# Revit family: QF_Vollrath_K1410-C
name_source: partatom
category: Specialty Equipment
revit_build: Autodesk Revit 2016 (Build: 20151007_0715(x64)
units: mm (PartAtom-declared; Revit-internal decimal feet)

## family parameters
Always vertical = Yes
Cut with Voids When Loaded = No
OmniClass Number = 23.40.40.14.31
OmniClass Title = Cleaning and Disposal Equipment
Part Type = Normal
Room Calculation Point = No
Round Connector Dimension = Use Diameter
Shared = No
Work Plane-Based = Yes

## types (1)
- QF_Vollrath_K1410-C
    Cold Water Size = 1"
    Default Elevation = 4' - 0"
    Depth = 1' - 3"
    Description = Wall-Mount Hand Sink
    Direct Waste Size = 2"
    Hot Water Size = 1"
    Manufacturer = Vollrath
    Model = K1410-C
    Sink Basin Depth = 0' - 5 1/2"
    Sink Depth = 0' - 9 1/16"
    Sink Width = 1' - 1 9/16"
    Weight in Pounds = 0
    Width = 1' - 5"

## geometry (parser evidence)
native form markers: Blend x39, Sweep x3
no freeform markers — native parametric forms only
